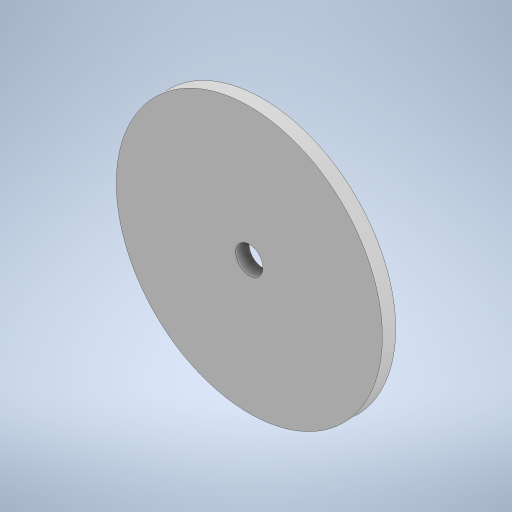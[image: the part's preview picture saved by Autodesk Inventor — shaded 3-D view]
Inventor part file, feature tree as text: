
AUTODESK INVENTOR PART (.ipt)
format: ipt  version: 2024 (Build 280153000, 153)  size: 214,016 bytes
history: native  units: mm
features: sketch x3, extrude x2
ambient origin geometry x8: Origin, YZ Plane, XZ Plane, XY Plane, X Axis, Y Axis, Z Axis, Center Point
bodies: Solid1 (feature_tree)
feature tree (5):
  extrude  "Extrusion1"  Depth=25.0mm TaperAngle=0.0deg
  extrude  "Extrusion2"  TaperAngle=0.0deg  [1 undecoded]
  sketch  "Sketch3"
  sketch  "Sketch1"  dims[d0=500.0mm d1=25.0mm d2=0.0mm]
  sketch  "Sketch2"  dims[d3=51.0mm d4=0.0mm d5=0.0mm]
note: 1 required parameter value undecoded (feature->parameter linkage not recoverable at this tier; creation-order binding heuristic only, values carry confidence <= 0.55)
